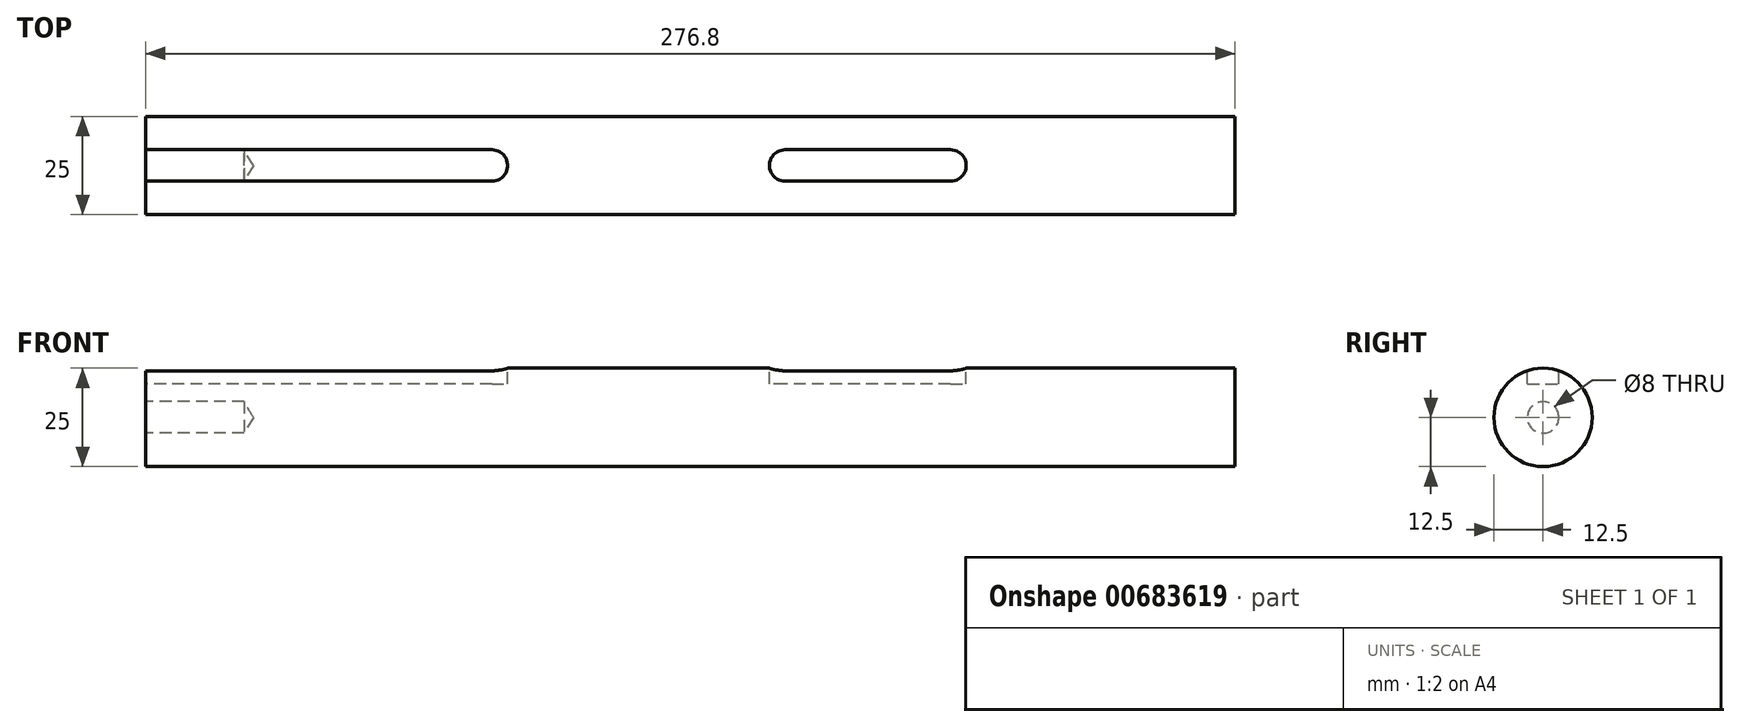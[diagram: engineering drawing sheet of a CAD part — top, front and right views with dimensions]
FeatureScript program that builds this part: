
annotation { "Feature Type Name" : "Feature", "Feature Type Description" : "" }
export const myFeature = defineFeature(function(context is Context, id is Id, definition is map)
    precondition{}
    {
        {
            var Q0;
            Q0=qCreatedBy(makeId("Front.planeOp"),FACE);
            var sketch = newSketch(context, id + "F0", { "sketchPlane" : qUnion([Q0])});
            skLineSegment(sketch, "E0", {"start": v(0, 0) * mm, "end": v(0, 12.5) * mm});
            skLineSegment(sketch, "E1", {"start": v(0, 12.5) * mm, "end": v(276.8, 12.5) * mm});
            skLineSegment(sketch, "E2", {"start": v(276.8, 12.5) * mm, "end": v(276.8, 0) * mm});
            skLineSegment(sketch, "E3", {"start": v(276.8, 0) * mm, "end": v(0, 0) * mm});
            skSolve(sketch);
        }
        {
            var Q0;
            Q0=qSketchRegion(id+"F0",true);
            var Q1;
            Q1=sQuery(id+"F0.wireOp",EDGE,"E3");
            revolve(context, id + "F1", {"entities" : qUnion([Q0]), "axis" : qUnion([Q1]), "revolveType" : RevolveType.FULL});
        }
        {
            var Q0;
            Q0=qCreatedBy(makeId("Top.planeOp"),FACE);
            cPlane(context, id + "F2", {"entities" : qUnion([Q0]), "cplaneType" : CPlaneType.OFFSET, "offset" : 12.5 * mm, "width" : 150 * mm, "height" : 150 * mm});
        }
        {
            var Q0;
            Q0=qCreatedBy(id+"F2.planeOp",FACE);
            var sketch = newSketch(context, id + "F3", { "sketchPlane" : qUnion([Q0])});
            skLineSegment(sketch, "E4", {"start": v(0, 0) * mm, "end": v(0, 4) * mm});
            skLineSegment(sketch, "E5", {"start": v(0, 4) * mm, "end": v(88, 4) * mm});
            skLineSegment(sketch, "E6", {"start": v(92, 0) * mm, "end": v(92, 0) * mm});
            skLineSegment(sketch, "E7", {"start": v(88, -4) * mm, "end": v(0, -4) * mm});
            skLineSegment(sketch, "E8", {"start": v(0, -4) * mm, "end": v(0, 0) * mm});
            skPoint(sketch, "E9.visualSharp", {"position": v(92, 4) * mm});
            skArc(sketch, "E9.filletArc", {"start": v(92, 0) * mm, "mid": v(90.83, 2.83) * mm, "end": v(88, 4) * mm});
            skPoint(sketch, "E10.visualSharp", {"position": v(92, -4) * mm});
            skArc(sketch, "E10.filletArc", {"start": v(88, -4) * mm, "mid": v(90.83, -2.83) * mm, "end": v(92, 0) * mm});
            skSolve(sketch);
        }
        {
            var Q0;
            Q0=qSketchRegion(id+"F3",true);
            extrude(context, id + "F4", {"entities" : qUnion([Q0]), "operationType" : NewBodyOperationType.REMOVE, "oppositeDirection" : true, "depth" : 4 * mm, "offsetDistance" : 25 * mm});
        }
        {
            var Q0;
            Q0=makeQuery(id+"F1.opRevolve","SWEPT_FACE",FACE,{"disambiguationData":[OSD([sQuery(id+"F0.wireOp",EDGE,"E0")])]});
            var sketch = newSketch(context, id + "F5", { "sketchPlane" : qUnion([Q0])});
            skCircle(sketch, "E11", {"center": v(0, 0) * mm, "radius": 4 * mm});
            skSolve(sketch);
        }
        {
            var Q0;
            Q0=sQuery(id+"F5.wireOp",VERTEX,"E11.center");
            var Q1;
            Q1=makeQuery(id+"F1.opRevolve","SWEPT_BODY",BODY,{"disambiguationData":[OSD([sQuery(id+"F0.wireOp",EDGE,"E0"),sQuery(id+"F0.wireOp",EDGE,"E1"),sQuery(id+"F0.wireOp",EDGE,"E2"),sQuery(id+"F0.wireOp",EDGE,"E3")])]});
            hole(context, id + "F6", {"style" : HoleStyle.SIMPLE, "endStyle" : HoleEndStyle.BLIND, "holeDiameter" : 8 * mm, "majorDiameter" : 5 * mm, "holeDepth" : 25 * mm, "isTappedThrough" : true, "tappedDepth" : 12 * mm, "tapClearance" : 3, "startFromSketch" : true, "locations" : qUnion([Q0]), "scope" : qUnion([Q1])});
        }
        {
            var Q0;
            Q0=qCreatedBy(id+"F2.planeOp",FACE);
            var sketch = newSketch(context, id + "F7", { "sketchPlane" : qUnion([Q0])});
            skLineSegment(sketch, "E12", {"start": v(208.5, 0) * mm, "end": v(208.5, 0) * mm});
            skLineSegment(sketch, "E13", {"start": v(204.5, 4) * mm, "end": v(162.5, 4) * mm});
            skLineSegment(sketch, "E14", {"start": v(158.5, 0) * mm, "end": v(158.5, 0) * mm});
            skLineSegment(sketch, "E15", {"start": v(162.5, -4) * mm, "end": v(204.5, -4) * mm});
            skPoint(sketch, "E16.visualSharp", {"position": v(208.5, 4) * mm});
            skArc(sketch, "E16.filletArc", {"start": v(208.5, 0) * mm, "mid": v(207.33, 2.83) * mm, "end": v(204.5, 4) * mm});
            skPoint(sketch, "E17.visualSharp", {"position": v(208.5, -4) * mm});
            skArc(sketch, "E17.filletArc", {"start": v(204.5, -4) * mm, "mid": v(207.33, -2.83) * mm, "end": v(208.5, 0) * mm});
            skPoint(sketch, "E18.visualSharp", {"position": v(158.5, 4) * mm});
            skArc(sketch, "E18.filletArc", {"start": v(162.5, 4) * mm, "mid": v(159.67, 2.83) * mm, "end": v(158.5, 0) * mm});
            skPoint(sketch, "E19.visualSharp", {"position": v(158.5, -4) * mm});
            skArc(sketch, "E19.filletArc", {"start": v(158.5, 0) * mm, "mid": v(159.67, -2.83) * mm, "end": v(162.5, -4) * mm});
            skLineSegment(sketch, "E20", {"start": v(158.5, 0) * mm, "end": v(208.5, 0) * mm, "construction": true});
            skLineSegment(sketch, "E21", {"start": v(183.5, 0) * mm, "end": v(183.5, 16.48) * mm, "construction": true});
            skLineSegment(sketch, "E22.0", {"start": v(231, 0) * mm, "end": v(231, 16.48) * mm, "construction": true});
            skLineSegment(sketch, "E23.0", {"start": v(136, 0) * mm, "end": v(136, 16.48) * mm, "construction": true});
            skSolve(sketch);
        }
        {
            var Q0;
            Q0=makeQuery(id+"F7.imprint","IMPRINT",FACE,{"disambiguationData":[TD([[makeQuery(id+"F7.imprint","IMPRINT",EDGE,{"derivedFrom":sQuery(id+"F7.wireOp",EDGE,"E13")}),1.0]])]});
            extrude(context, id + "F8", {"entities" : qUnion([Q0]), "operationType" : NewBodyOperationType.REMOVE, "oppositeDirection" : true, "depth" : 4 * mm, "offsetDistance" : 25 * mm});
        }
    });
